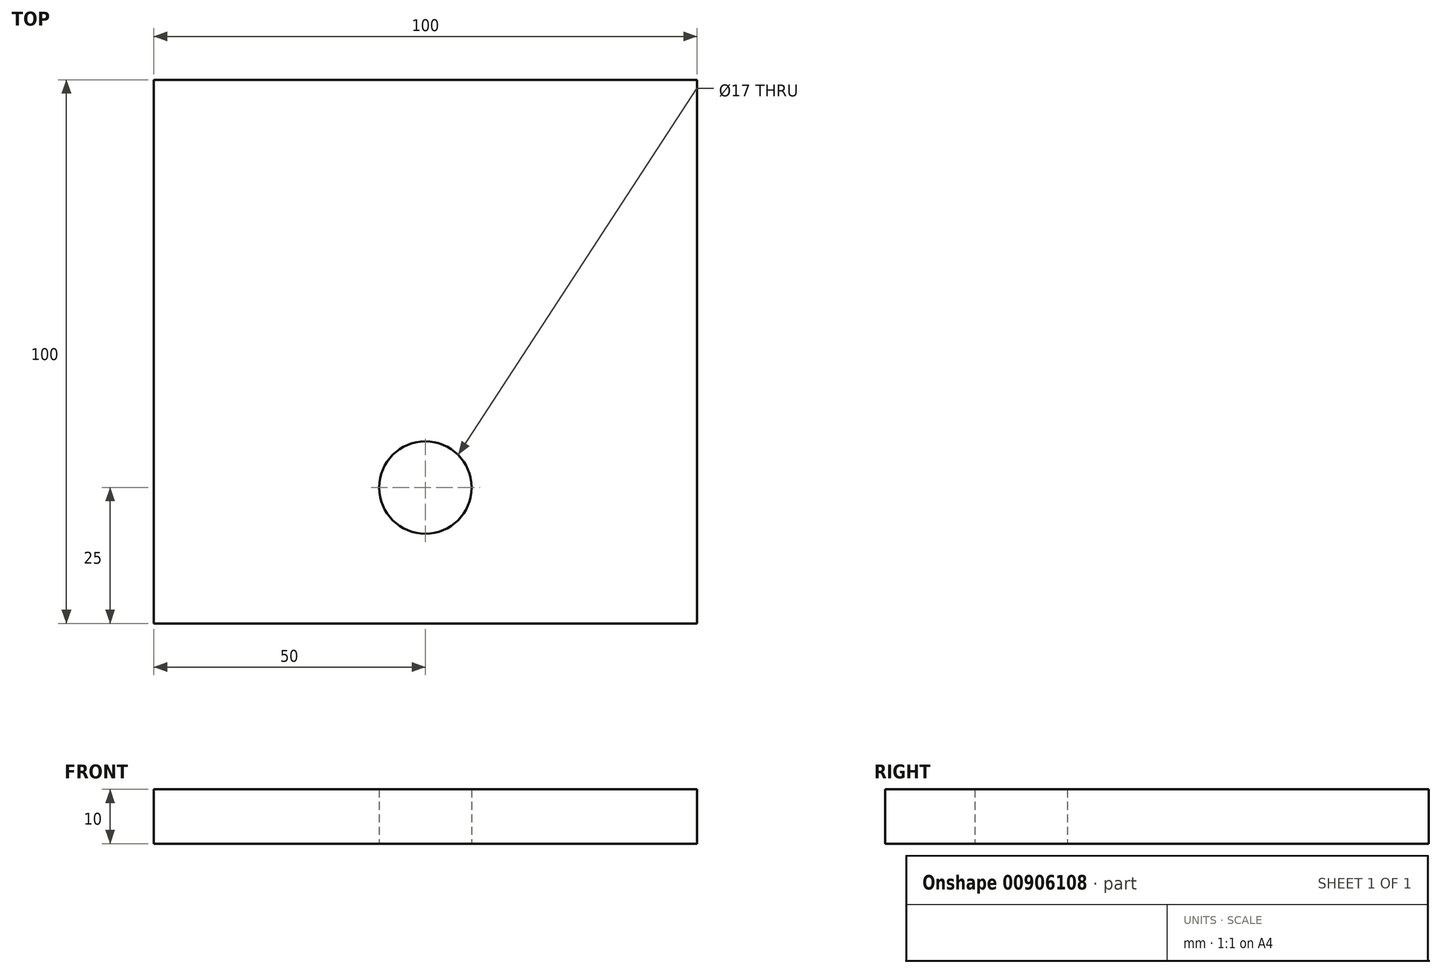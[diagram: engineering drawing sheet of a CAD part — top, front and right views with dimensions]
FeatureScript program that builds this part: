
annotation { "Feature Type Name" : "Feature", "Feature Type Description" : "" }
export const myFeature = defineFeature(function(context is Context, id is Id, definition is map)
    precondition{}
    {
        {
            var Q0;
            Q0=qCreatedBy(makeId("Top.planeOp"),FACE);
            var sketch = newSketch(context, id + "F0", { "sketchPlane" : qUnion([Q0])});
            skLineSegment(sketch, "E0.bottom", {"start": v(0, 0) * mm, "end": v(100, 0) * mm});
            skLineSegment(sketch, "E0.top", {"start": v(0, 100) * mm, "end": v(100, 100) * mm});
            skLineSegment(sketch, "E0.left", {"start": v(0, 0) * mm, "end": v(0, 100) * mm});
            skLineSegment(sketch, "E0.right", {"start": v(100, 0) * mm, "end": v(100, 100) * mm});
            skSolve(sketch);
        }
        {
            var Q0;
            Q0 = qSketchRegion(id + "F0", true);
            extrude(context, id + "F1", {"entities" : qUnion([Q0]), "depth" : 10 * mm, "offsetDistance" : 25 * mm});
        }
        {
            var Q0;
            Q0=makeQuery(id+"F1.opExtrude","CAP_FACE",FACE,{"disambiguationData":[OSD([sQuery(id+"F0.wireOp",EDGE,"E0.bottom"),sQuery(id+"F0.wireOp",EDGE,"E0.top"),sQuery(id+"F0.wireOp",EDGE,"E0.left"),sQuery(id+"F0.wireOp",EDGE,"E0.right")])],"isStart":true});
            var sketch = newSketch(context, id + "F2", { "sketchPlane" : qUnion([Q0])});
            skCircle(sketch, "E1", {"center": v(50, -25) * mm, "radius": 8.5 * mm});
            skSolve(sketch);
        }
        {
            var Q0;
            Q0 = qSketchRegion(id + "F2", true);
            extrude(context, id + "F3", {"entities" : qUnion([Q0]), "operationType" : NewBodyOperationType.REMOVE, "oppositeDirection" : true, "depth" : 25 * mm, "offsetDistance" : 25 * mm});
        }
    });
